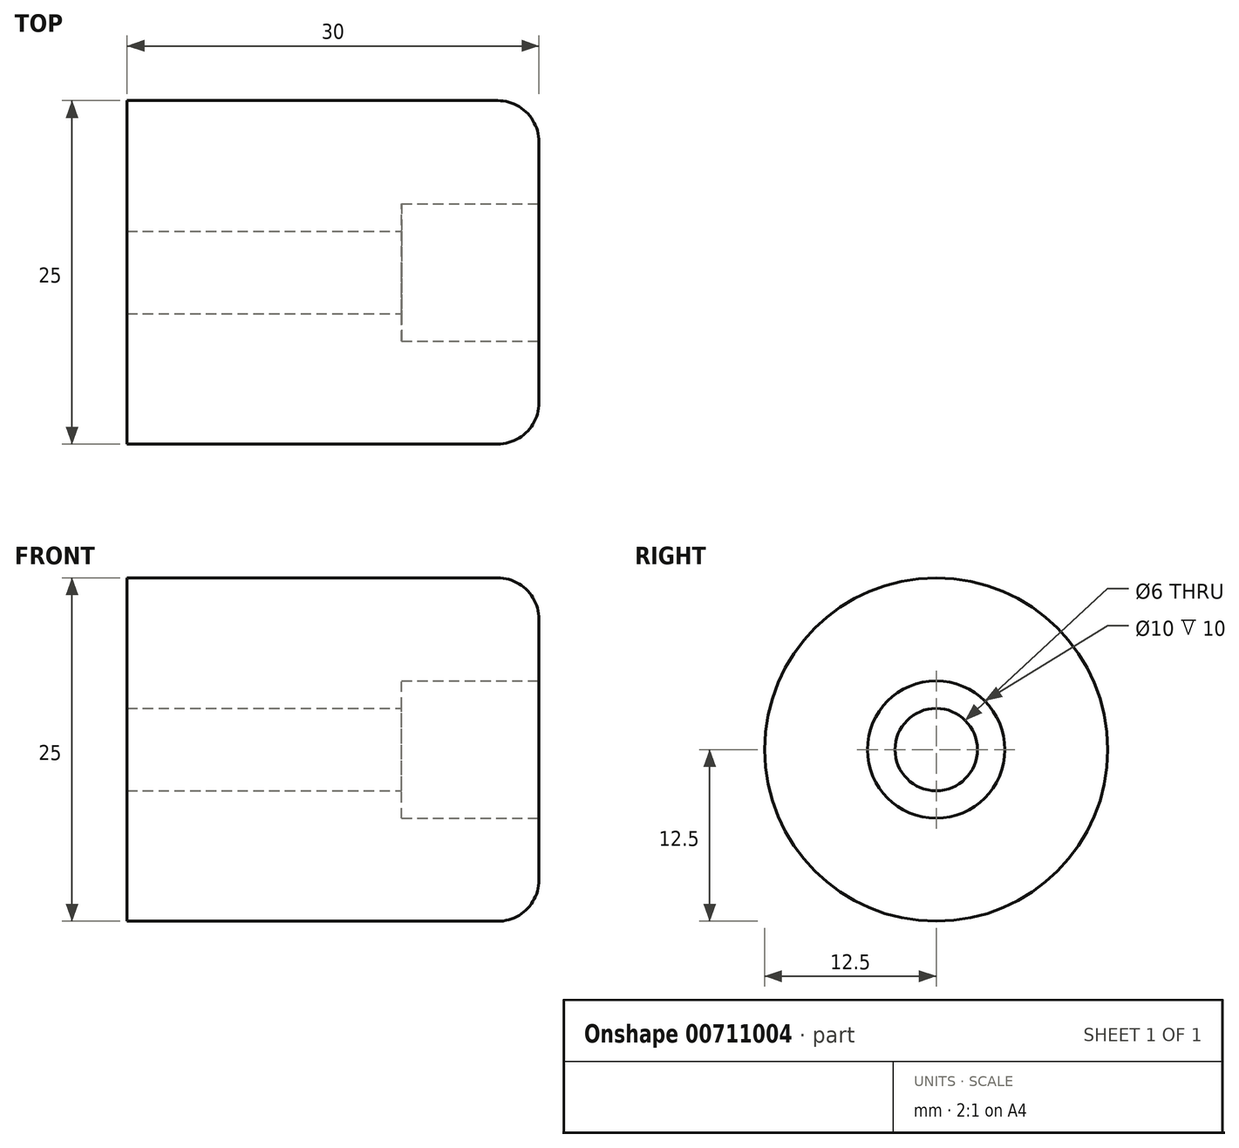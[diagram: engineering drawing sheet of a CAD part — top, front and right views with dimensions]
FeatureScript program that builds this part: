
annotation { "Feature Type Name" : "Feature", "Feature Type Description" : "" }
export const myFeature = defineFeature(function(context is Context, id is Id, definition is map)
    precondition{}
    {
        {
            var Q0;
            Q0=qCreatedBy(makeId("Right.planeOp"),FACE);
            var sketch = newSketch(context, id + "F0", { "sketchPlane" : qUnion([Q0])});
            skCircle(sketch, "E0", {"center": v(0, 0) * mm, "radius": 12.5 * mm});
            skSolve(sketch);
        }
        {
            var Q0;
            Q0=makeQuery(id+"F0.imprint","IMPRINT",FACE,{"disambiguationData":[TD([[makeQuery(id+"F0.imprint","IMPRINT",EDGE,{"derivedFrom":sQuery(id+"F0.wireOp",EDGE,"E0")}),1.0]])]});
            extrude(context, id + "F1", {"entities" : qUnion([Q0]), "depth" : 30 * mm, "offsetDistance" : 25 * mm});
        }
        {
            var Q0;
            Q0=makeQuery(id+"F1.opExtrude","CAP_EDGE",EDGE,{"disambiguationData":[OSD([sQuery(id+"F0.wireOp",EDGE,"E0")])],"isStart":false});
            fillet(context, id + "F2", {"entities" : qUnion([Q0]), "radius" : 3 * mm, "tangentPropagation" : true, "allowEdgeOverflow" : false});
        }
        {
            var Q0;
            Q0=makeQuery(id+"F1.opExtrude","CAP_FACE",FACE,{"disambiguationData":[OSD([sQuery(id+"F0.wireOp",EDGE,"E0")])],"isStart":false});
            var sketch = newSketch(context, id + "F3", { "sketchPlane" : qUnion([Q0])});
            skPoint(sketch, "E1", {"position": v(0, 0) * mm});
            skSolve(sketch);
        }
        {
            var Q0;
            Q0=sQuery(id+"F3.wireOp",VERTEX,"E1");
            var Q1;
            Q1=makeQuery(id+"F1.opExtrude","SWEPT_BODY",BODY,{"disambiguationData":[OSD([sQuery(id+"F0.wireOp",EDGE,"E0")])]});
            hole(context, id + "F4", {"style" : HoleStyle.C_BORE, "endStyle" : HoleEndStyle.THROUGH, "holeDiameter" : 6 * mm, "cBoreDiameter" : 10 * mm, "cBoreDepth" : 10 * mm, "majorDiameter" : 5 * mm, "isTappedThrough" : true, "tappedDepth" : 12 * mm, "tapClearance" : 3, "locations" : qUnion([Q0]), "scope" : qUnion([Q1])});
        }
    });
